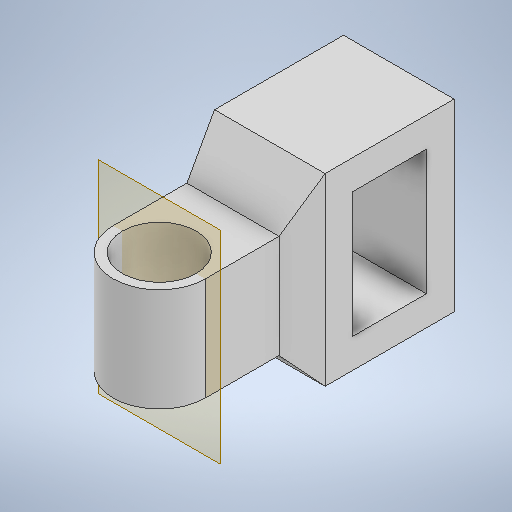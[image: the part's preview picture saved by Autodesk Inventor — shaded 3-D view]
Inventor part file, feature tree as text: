
AUTODESK INVENTOR PART (.ipt)
format: ipt  version: 2025.2 (Build 292293000, 293)  size: 276,480 bytes
history: native  units: mm
features: extrude x6, sketch x6, other x2, plane x1, loft x1
ambient origin geometry x8: Origin, YZ Plane, XZ Plane, XY Plane, X Axis, Y Axis, Z Axis, Center Point
bodies: Solid1 (feature_tree)
feature tree (16):
  extrude  "Extrusion1"  Depth=25.0mm
  extrude  "Extrusion2"  Depth=20.0mm TaperAngle=0.0deg
  extrude  "Extrusion3"  Depth=10.0mm
  plane  "Work Plane1"
  extrude  "Extrusion4"  Depth=30.0mm
  extrude  "Extrusion5"  Depth=30.0mm
  extrude  "Extrusion6"  Depth=20.0mm TaperAngle=0.0deg
  loft  "Loft2"
  sketch  "Sketch1"  dims[d0=20.0mm d1=25.0mm]
  sketch  "Sketch2"  dims[d2=28.0mm d3=0.0mm d4=20.0mm d5=0.0mm]
  sketch  "Sketch3"  dims[d6=50.0mm d7=0.0mm d8=10.0mm]
  sketch  "Sketch4"  dims[d9=30.0mm d10=32.0mm]
  sketch  "Sketch5"  dims[d11=15.0mm d12=0.0mm d17=30.0mm]
  sketch  "Sketch7"  dims[d18=50.0mm d19=20.0mm d20=0.0mm d21=15.0mm d22=0.0mm d23=20.0mm d24=34.0mm d25=30.0mm d26=0.0mm d27=0.0mm d28=90.0deg d29=0.0mm d30=90.0deg]
  other  "Edges3"
  other  "Edges4"
